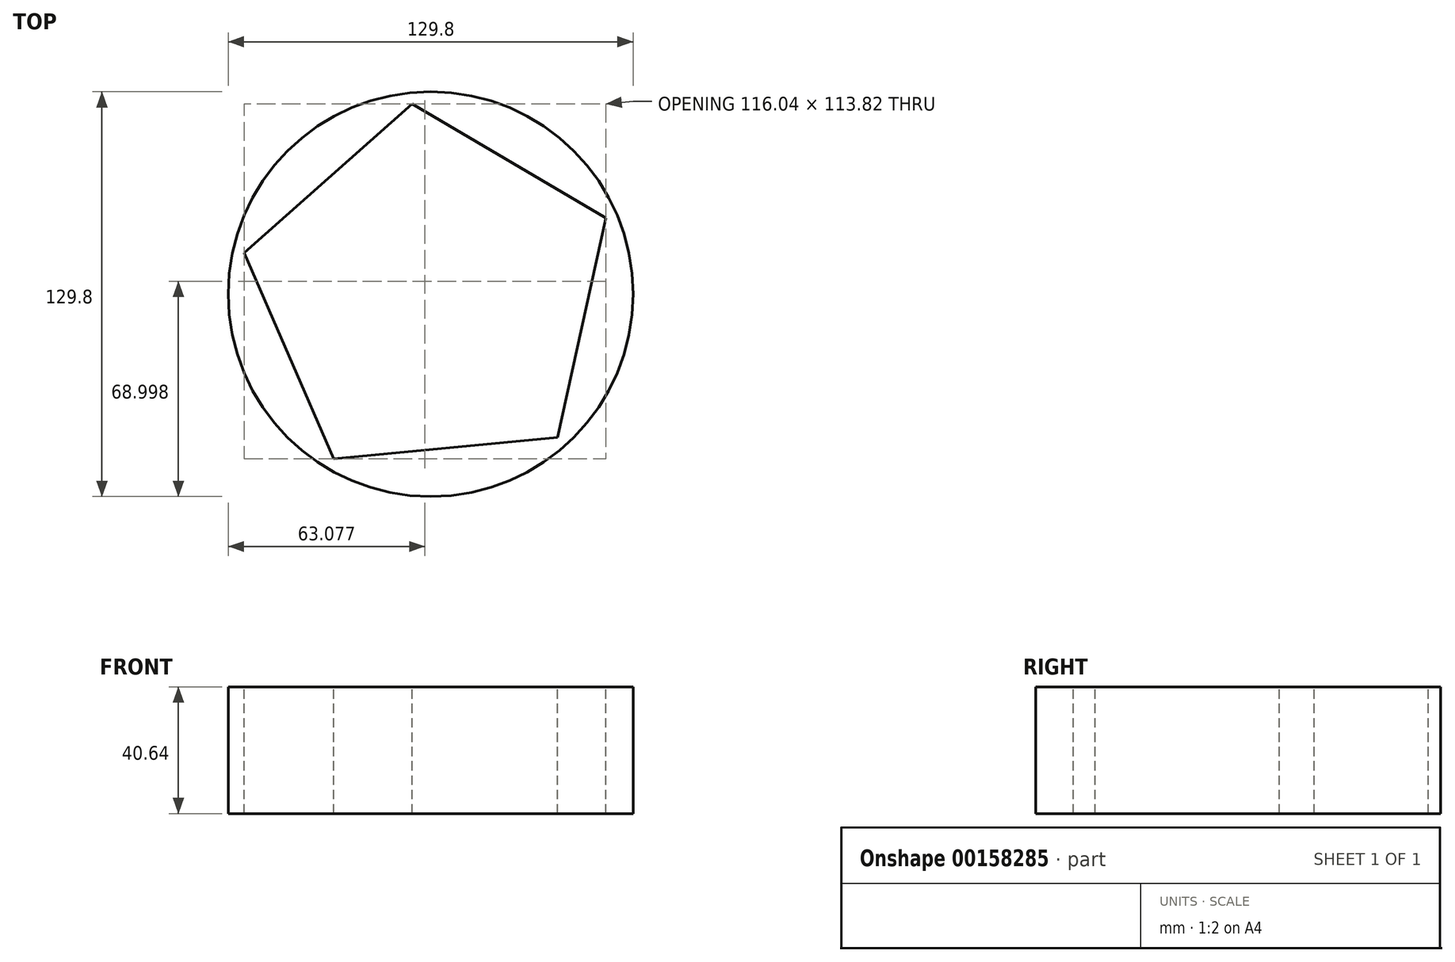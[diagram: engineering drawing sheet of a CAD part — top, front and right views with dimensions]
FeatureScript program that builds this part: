
annotation { "Feature Type Name" : "Feature", "Feature Type Description" : "" }
export const myFeature = defineFeature(function(context is Context, id is Id, definition is map)
    precondition{}
    {
        {
            var Q0;
            Q0=qCreatedBy(makeId("Top.planeOp"),FACE);
            var sketch = newSketch(context, id + "F0", { "sketchPlane" : qUnion([Q0])});
            skCircle(sketch, "E0", {"center": v(-36.62, 29.24) * mm, "radius": 64.9 * mm});
            skCircle(sketch, "E1.cCircle", {"center": v(-36.62, 29.24) * mm, "radius": 49.58 * mm, "construction": true});
            skLineSegment(sketch, "E1.0", {"start": v(-96.46, 42.5) * mm, "end": v(-42.51, 90.25) * mm});
            skLineSegment(sketch, "E1.1", {"start": v(-42.51, 90.25) * mm, "end": v(19.58, 53.7) * mm});
            skLineSegment(sketch, "E1.2", {"start": v(19.58, 53.7) * mm, "end": v(4, -16.65) * mm});
            skLineSegment(sketch, "E1.3", {"start": v(4, -16.65) * mm, "end": v(-67.72, -23.57) * mm});
            skLineSegment(sketch, "E1.4", {"start": v(-67.72, -23.57) * mm, "end": v(-96.46, 42.5) * mm});
            skPoint(sketch, "E1.0.midPoint", {"position": v(-69.49, 66.37) * mm});
            skSolve(sketch);
        }
        {
            var Q0;
            Q0 = qSketchRegion(id + "F0", true);
            extrude(context, id + "F1", {"entities" : qUnion([Q0]), "oppositeDirection" : true, "depth" : 40.64 * mm});
        }
    });
